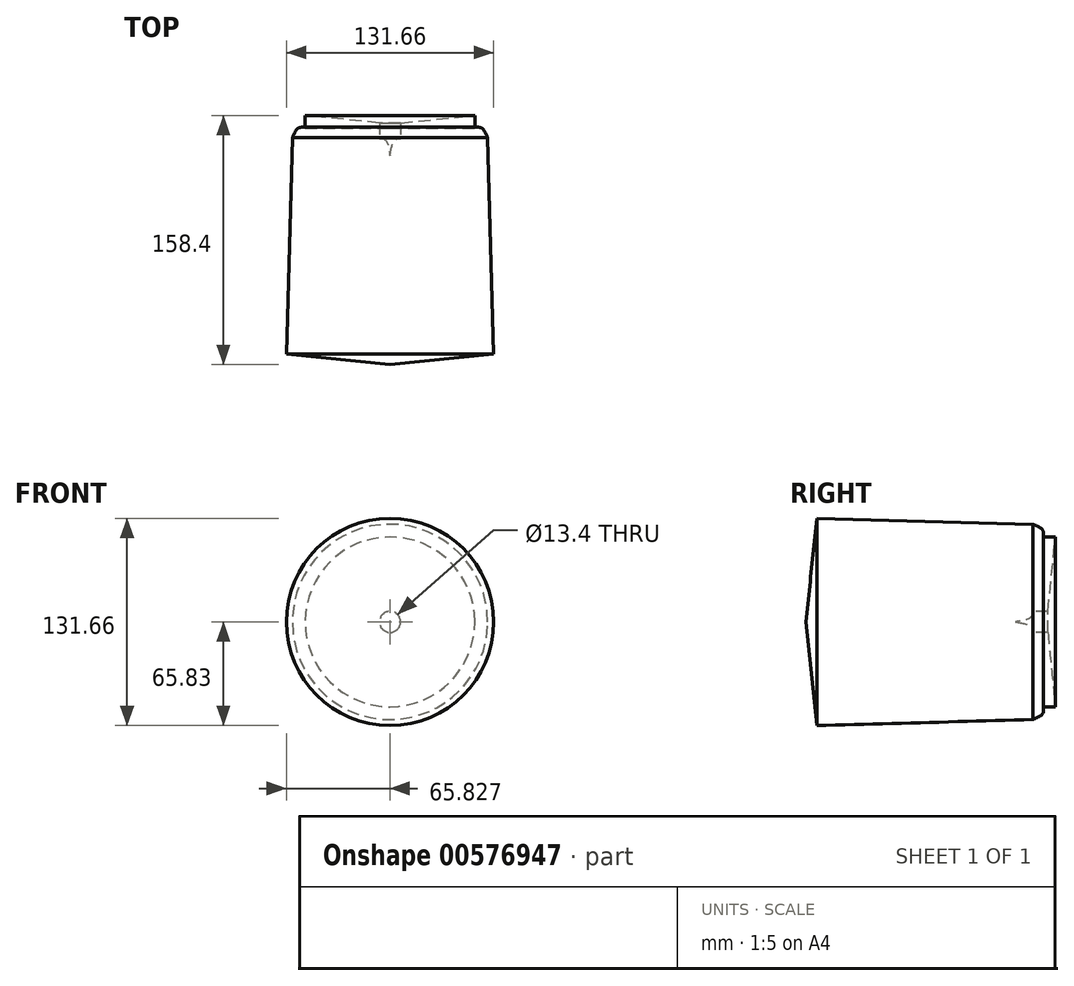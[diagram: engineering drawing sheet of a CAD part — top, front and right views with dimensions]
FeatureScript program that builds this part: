
annotation { "Feature Type Name" : "Feature", "Feature Type Description" : "" }
export const myFeature = defineFeature(function(context is Context, id is Id, definition is map)
    precondition{}
    {
        {
            var Q0;
            Q0=qCreatedBy(makeId("Top.planeOp"),FACE);
            var sketch = newSketch(context, id + "F0", { "sketchPlane" : qUnion([Q0])});
            skLineSegment(sketch, "E0", {"start": v(-115.57, -75.98) * mm, "end": v(-115.57, 57.03) * mm});
            skFitSpline(sketch, "E1", {"points": [v(-115.57, 57.03) * mm, v(-112.58, 66.82) * mm, v(-108.87, 67.82) * mm], "startDerivative": vector(3.3, 19.87) * mm, "endDerivative": vector(10.7, 0.12) * mm});
            skLineSegment(sketch, "E2", {"start": v(-108.87, 67.82) * mm, "end": v(-108.87, 77.6) * mm});
            skLineSegment(sketch, "E3", {"start": v(-108.87, 77.6) * mm, "end": v(-61.66, 82.42) * mm});
            skLineSegment(sketch, "E4", {"start": v(-61.66, 82.42) * mm, "end": v(-61.66, 74.45) * mm});
            skFitSpline(sketch, "E5", {"points": [v(-61.66, 74.45) * mm, v(-57.47, 74.45) * mm, v(-53.53, 68.24) * mm], "startDerivative": vector(10.35, 2.34) * mm, "endDerivative": vector(6.1, -14) * mm});
            skLineSegment(sketch, "E6", {"start": v(-53.53, 68.24) * mm, "end": v(-49.74, -69.2) * mm});
            skLineSegment(sketch, "E7", {"start": v(-49.74, -69.2) * mm, "end": v(-115.57, -75.98) * mm});
            skSolve(sketch);
        }
        {
            var Q0;
            Q0 = qSketchRegion(id + "F0", true);
            var Q1;
            Q1=sQuery(id+"F0.wireOp",EDGE,"E0");
            revolve(context, id + "F1", {"entities" : qUnion([Q0]), "axis" : qUnion([Q1]), "revolveType" : RevolveType.FULL});
        }
    });
